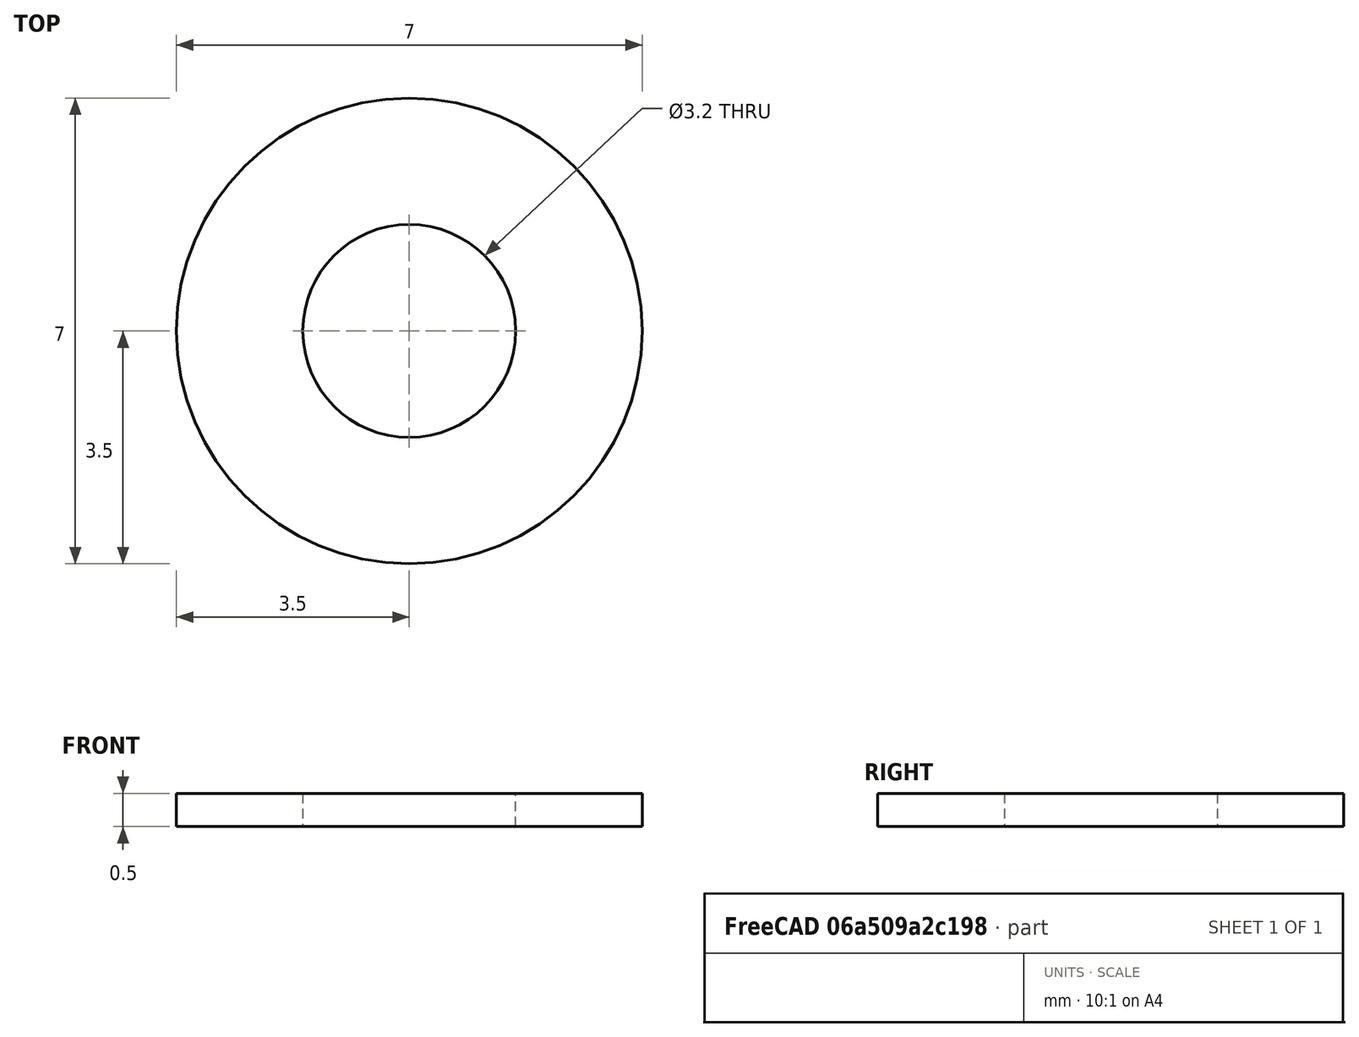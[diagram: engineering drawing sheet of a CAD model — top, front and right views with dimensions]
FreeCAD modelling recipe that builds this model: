
FCSTD DOCUMENT  (FreeCAD 0.15R4671 (Git))
Label: ISO7090_M3_flat_washer
License: Public Domain
LicenseURL: http://en.wikipedia.org/wiki/Public_domain
objects: Sketcher::SketchObject×1, PartDesign::Pad×1
note: 3 computed .brp shape members not serialized (recipe doc carries the construction recipe); baked Part::Feature solids carry a one-line shape summary decoded from their .brp

FEATURE [Sketcher::SketchObject] Sketch
  sketch-geometry (6):
    g0: Circle CenterX=0 CenterY=0 CenterZ=0 NormalX=0 NormalY=0 NormalZ=1 Radius=1.6
    g1: Circle CenterX=0 CenterY=0 CenterZ=0 NormalX=0 NormalY=0 NormalZ=1 Radius=3.5
    g2: GeomPoint [constr] X=0 Y=3.5 Z=0
    g3: GeomPoint [constr] X=0 Y=1.6 Z=0
    g4: GeomPoint [constr] X=0 Y=-1.6 Z=0
    g5: GeomPoint [constr] X=0 Y=-3.5 Z=0
  constraints (12):
    c: Coincident(g0,g-1)
    c: Coincident(g1,g-1)
    c: PointOnObject(g2,g-2)
    c: PointOnObject(g3,g-2)
    c: PointOnObject(g4,g-2)
    c: PointOnObject(g5,g-2)
    c: PointOnObject(g2,g1)
    c: PointOnObject(g3,g0)
    c: PointOnObject(g4,g0)
    c: PointOnObject(g5,g1)
    c: DistanceY(g3,g4) = -3.2
    c: DistanceY(g2,g5) = -7
FEATURE [PartDesign::Pad] Pad
  Length = 0.5
  Length2 = 100
  Sketch = -> Sketch
  Type = 0
